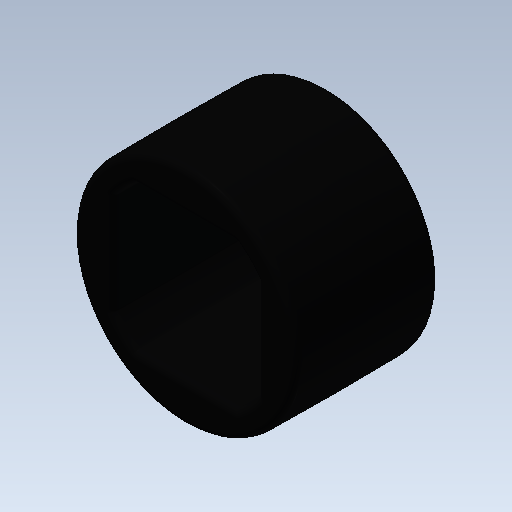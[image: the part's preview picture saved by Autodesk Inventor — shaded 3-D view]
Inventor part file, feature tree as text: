
AUTODESK INVENTOR PART (.ipt)
format: ipt  version: 2020 (Build 240168000, 168)  size: 254,976 bytes
history: native  units: in
note: dims shown in document units (in); Inventor stores cm internally (conversion verified against a paired STEP export)
features: fillet x1, other x1, imported_body x1
ambient origin geometry x8: Origin, YZ Plane, XZ Plane, XY Plane, X Axis, Y Axis, Z Axis, Center Point
bodies: Body1 (feature_tree)
feature tree (3):
  fillet  "Fillet1"  [1 undecoded]
  other  "Spacer HS 0.5 unit"
  imported_body  "Base1"
note: 1 required parameter value undecoded (feature->parameter linkage not recoverable at this tier; creation-order binding heuristic only, values carry confidence <= 0.55)
